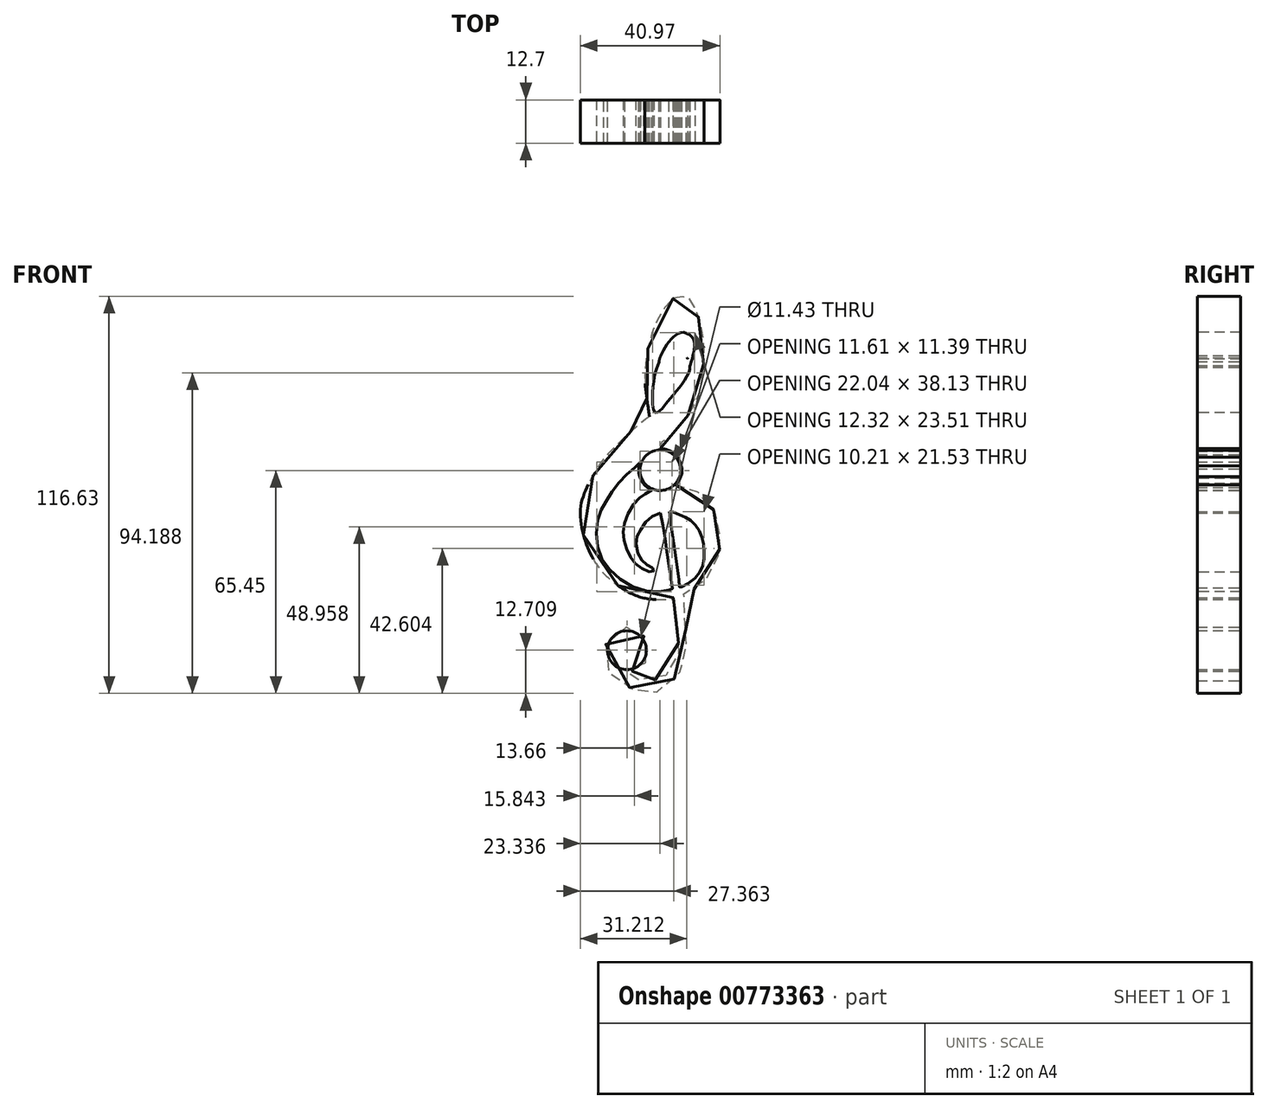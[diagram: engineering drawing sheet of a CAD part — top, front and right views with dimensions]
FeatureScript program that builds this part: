
annotation { "Feature Type Name" : "Feature", "Feature Type Description" : "" }
export const myFeature = defineFeature(function(context is Context, id is Id, definition is map)
    precondition{}
    {
        {
            var Q0;
            Q0=qCreatedBy(makeId("Front.planeOp"),FACE);
            var sketch = newSketch(context, id + "F0", { "sketchPlane" : qUnion([Q0])});
            skCircle(sketch, "E0", {"center": v(0, 0) * mm, "radius": 6.35 * mm});
            skFitSpline(sketch, "E1", {"points": [v(6.31, -36.93) * mm, v(9.78, -35.03) * mm, v(13.89, -31.56) * mm, v(16.25, -27.46) * mm, v(17.43, -23.37) * mm, v(17.52, -20.78) * mm, v(17.52, -18.63) * mm, v(17.27, -16.1) * mm, v(15.15, -10.6) * mm, v(11.7, -6.89) * mm, v(8.05, -5.03) * mm, v(4.61, -4.37) * mm, v(6.05, -1.93) * mm, v(6.23, 1.25) * mm, v(5.12, 3.76) * mm, v(2.53, 5.82) * mm, v(0, 6.35) * mm, v(0, 7.7) * mm, v(3.41, 10.53) * mm, v(6.6, 14.04) * mm, v(9.72, 18.68) * mm, v(11.78, 23.64) * mm, v(12.66, 29.84) * mm, v(12.86, 35.61) * mm, v(12.46, 39.73) * mm, v(11.62, 43.83) * mm, v(10.21, 47.54) * mm, v(8.62, 50.35) * mm, v(7.07, 50.76) * mm, v(4.67, 50.96) * mm, v(1.25, 47.63) * mm, v(-1.94, 41.67) * mm, v(-3.68, 35.29) * mm, v(-4.38, 31.02) * mm, v(-4.48, 26.2) * mm, v(-3.83, 20.29) * mm, v(-3.17, 15.88) * mm, v(-3.17, 15.78) * mm, v(-5.05, 14.37) * mm, v(-8.14, 11.75) * mm, v(-11.8, 8.37) * mm, v(-17.34, 2.36) * mm, v(-20.81, -3.55) * mm, v(-23.25, -10.12) * mm, v(-22.65, -18.68) * mm, v(-19.93, -25.63) * mm, v(-15.74, -31.17) * mm, v(-7.04, -36.86) * mm, v(0, -37.98) * mm, v(3.79, -37.53) * mm, v(4, -37.42) * mm, v(4, -39.43) * mm, v(4.9, -44.67) * mm, v(5.35, -50.92) * mm, v(5.24, -54.46) * mm, v(3.2, -58.88) * mm, v(-1.23, -61.56) * mm, v(-6.67, -61.49) * mm, v(-9.43, -60.14) * mm, v(-10.38, -59.2) * mm, v(-8.1, -59.04) * mm, v(-4.94, -57.38) * mm, v(-3.51, -54.07) * mm, v(-4.15, -49.89) * mm, v(-6.67, -46.89) * mm, v(-10.46, -46.18) * mm, v(-14.8, -49.1) * mm, v(-16.53, -53.99) * mm, v(-14.96, -59.67) * mm, v(-9.9, -63.38) * mm, v(-5.17, -65.32) * mm, v(-1.54, -65.32) * mm, v(3.35, -62.12) * mm, v(7.14, -56.99) * mm, v(7.69, -52.33) * mm, v(7.45, -46.02) * mm, v(6.66, -40.73) * mm, v(6.31, -36.93) * mm]});
            skFitSpline(sketch, "E2", {"points": [v(-5.86, 2.44) * mm, v(-6.34, 0.38) * mm, v(-6.26, -1.08) * mm, v(-5.86, -2.44) * mm, v(-4.94, -3.99) * mm, v(-3.84, -5.06) * mm, v(-2.53, -5.82) * mm], "startDerivative": vector(-3.24, -11.29) * mm, "endDerivative": vector(8.4, -4.47) * mm});
            skFitSpline(sketch, "E3", {"points": [v(2.67, -12.21) * mm, v(5.12, -12.83) * mm, v(8.64, -14.5) * mm, v(11.54, -17.85) * mm, v(12.82, -22.48) * mm, v(12.55, -27.67) * mm, v(9.76, -32.08) * mm, v(5.8, -34.47) * mm, v(5.68, -33.86) * mm, v(2.84, -13.72) * mm, v(2.78, -13) * mm, v(2.67, -12.21) * mm]});
            skFitSpline(sketch, "E4", {"points": [v(-5.86, 2.44) * mm, v(-7.37, 0.86) * mm, v(-10.52, -1.96) * mm, v(-13.58, -5.5) * mm, v(-16.2, -9.59) * mm, v(-17.71, -12.5) * mm, v(-18.72, -17.75) * mm, v(-17.93, -24.11) * mm, v(-14.7, -29.36) * mm, v(-9.12, -33.7) * mm, v(-2.2, -35.72) * mm, v(2.26, -35.27) * mm, v(3.71, -35.05) * mm, v(3.6, -34.94) * mm, v(3.16, -32.15) * mm, v(2.15, -25.12) * mm, v(1.15, -18.42) * mm, v(0, -12.5) * mm], "startDerivative": vector(-31.99, -35.89) * mm, "endDerivative": vector(-17.48, 84.57) * mm});
            skFitSpline(sketch, "E5", {"points": [v(0, -12.5) * mm, v(-3.54, -14.45) * mm, v(-5.86, -17.64) * mm, v(-7.11, -20.43) * mm, v(-6.43, -24.57) * mm, v(-4.9, -27.02) * mm, v(-2.77, -28.44) * mm, v(-1.9, -29.15) * mm, v(-2.02, -29.7) * mm, v(-3.08, -29.86) * mm, v(-6.07, -28.36) * mm, v(-8.37, -26.23) * mm, v(-10.14, -22.17) * mm, v(-10.85, -18.58) * mm, v(-10.18, -14.45) * mm, v(-7.17, -9.22) * mm, v(-4.94, -7.3) * mm, v(-2.53, -5.82) * mm], "startDerivative": vector(-56.08, -23.16) * mm, "endDerivative": vector(43.51, 25.74) * mm});
            skCircle(sketch, "E6", {"center": v(0, 0) * mm, "radius": 5.96 * mm});
            skFitSpline(sketch, "E7", {"points": [v(-5.86, 2.44) * mm, v(-5.12, 3.05) * mm, v(-3.83, 4.57) * mm, v(-2.13, 5.57) * mm, v(0, 5.96) * mm, v(2.53, 5.82) * mm], "startDerivative": vector(5.07, 3.46) * mm, "endDerivative": vector(11.08, -1.1) * mm});
            skCircle(sketch, "E8", {"center": v(-9.78, -52.87) * mm, "radius": 5.72 * mm});
            skCircle(sketch, "E9", {"center": v(4.22, 31.4) * mm, "radius": 4.03 * mm});
            skFitSpline(sketch, "E10", {"points": [v(0.36, 32.58) * mm, v(1.1, 33.97) * mm, v(2.37, 35) * mm, v(3.72, 35.4) * mm, v(5.3, 35.29) * mm, v(6.45, 34.76) * mm, v(7.33, 33.97) * mm, v(7.9, 33.03) * mm, v(8.04, 32.68) * mm, v(8.24, 31.21) * mm, v(7.55, 29.14) * mm, v(6.39, 28.01) * mm, v(4.97, 27.45) * mm, v(2.85, 27.62) * mm, v(1.24, 28.7) * mm, v(0.3, 30.42) * mm, v(0.36, 32.58) * mm]});
            skCircle(sketch, "E11", {"center": v(4.22, 31.4) * mm, "radius": 4.58 * mm});
            skFitSpline(sketch, "E12", {"points": [v(4.5, 39.57) * mm, v(2.76, 38.07) * mm, v(1.18, 35.67) * mm, v(0.22, 33.65) * mm, v(-0.35, 31.84) * mm, v(-1.22, 29.47) * mm, v(-1.9, 26.28) * mm, v(-2.24, 20.29) * mm, v(-1.38, 16.85) * mm, v(2.37, 20.29) * mm, v(5.33, 23.95) * mm, v(7.54, 27.03) * mm, v(8.64, 29.55) * mm, v(8.64, 30.2) * mm, v(9.38, 32.74) * mm, v(9.9, 35) * mm, v(10.04, 37.9) * mm, v(8.64, 39.73) * mm, v(6.39, 40.48) * mm, v(4.5, 39.57) * mm]});
            skFitSpline(sketch, "E13", {"points": [v(0.22, 33.65) * mm, v(1.79, 35.3) * mm, v(3.63, 35.95) * mm, v(5.91, 35.67) * mm, v(7.07, 35) * mm, v(8.22, 33.65) * mm, v(8.76, 31.99) * mm, v(8.75, 30.75) * mm], "startDerivative": vector(9.15, 11.59) * mm, "endDerivative": vector(-0.74, -10) * mm});
            skFitSpline(sketch, "E14", {"points": [v(-0.38, 31.85) * mm, v(-0.25, 30.4) * mm, v(1.14, 28.01) * mm, v(2.76, 27.06) * mm, v(4.85, 26.87) * mm, v(6.39, 27.37) * mm, v(7.91, 28.7) * mm, v(8.64, 29.55) * mm], "startDerivative": vector(-0.4, -10.48) * mm, "endDerivative": vector(5.63, 7.14) * mm});
            skSolve(sketch);
        }
        {
            var Q0;
            Q0 = qSketchRegion(id + "F0", true);
            var Q1;
            {var subQ4=sQuery(id+"F0.wireOp",EDGE,"E10");var subQ5=sQuery(id+"F0.wireOp",EDGE,"E9");var subQ32=makeQuery(id+"F0.imprint","INTERSECT",VERTEX,{"disambiguationData":[OD(6.0)],"derivedFrom":[subQ5,subQ4]});Q1=makeQuery(id+"F0.imprint","IMPRINT",FACE,{"disambiguationData":[TD([[makeQuery(id+"F0.imprint","IMPRINT",EDGE,{"disambiguationData":[TD([[subQ32,-1.0]])],"derivedFrom":subQ5}),-1.0]])]});}
            extrude(context, id + "F1", {"entities" : qUnion([Q0, Q1]), "depth" : 12.7 * mm, "offsetDistance" : 25.4 * mm});
        }
    });
